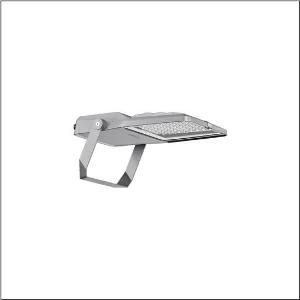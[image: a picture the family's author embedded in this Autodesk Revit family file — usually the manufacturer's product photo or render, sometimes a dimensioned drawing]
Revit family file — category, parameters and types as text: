
# Revit family: floodlight_fl_21_mini___pl52_5xa7775b2d1a_29c3
name_source: partatom
category: Lighting Fixtures
units: mm (PartAtom-declared; Revit-internal decimal feet)

## family parameters
Cut with Voids When Loaded = No
Host = Face
Light Source = No
Part Type = Normal
Room Calculation Point = No
Round Connector Dimension = Use Diameter
Shared = No

## types (1)
- --- (1 x LED, 6230 lm, 45.7 W, 3000K)
    Apparent Load = 46 VA
    CIE Flux Codes = 26 60 98 100 100
    Color Rendering = 70
    Color Temperature = 3000K
    Default Elevation = 1800 mm
    Description = Floodlight FL 21 mini, floodlight, primary light control with lens, of PMMA, primary optical cover: protective disc, of toughened safety glass, transparent, light distribution: PL52, light emission: direct distribution, installation type: surface-mounted, LED, High Power LED, rated luminous flux: 6.230lm, luminous efficacy: 136lm/W, light colour: 730, colour temperature: 3000K, control: flexible luminous flux parameterisation, time-dependent luminous flux control, constant luminous flux control, overheat protection, presetting dimming logarithmic, with terminal, 6-pole, mains connection: 220..240V, AC, 50/60Hz, start of lifetime: 46W, end of service life: 48W, reduction: 22W, luminaire housing, of diecast aluminium, powder-coated, Siteco® metallic grey (DB 702S), corrosivity category C5 mid according to DIN EN ISO 12944, sealing non-destructively replaceable, mounting bracket, of steel, galvanised, powder-coated, Siteco® metallic grey (DB 702S), Smart Interface above, protection rating (complete): IP66, insulation class (complete): insulation class II (safety insulation), certification: CE, ENEC, VDE, protection symbol: D, impact resistance: IK08, permissible operating ambient temperature: -40..+40°C, permissible operating ambient temperature for outdoor applications: -40..+50°C, standard: DIN EN 12944, LABS conformity tested according to VDMA 24364:2018-05, packaging unit: 1 piece

Light Distribution: PL52
    Height = 70 mm
    Lamp = 1 x LED
    Lamp Light Flux = 6230 lm
    Lamp Power = 45.7 W
    Lamp count = 1
    Length = 485 mm
    Luminous efficacy = 136 lm/W
    Manufacturer = Siteco
    ModVariant = No
    Model = 5XA7775B2D1A
    Number of Poles = 1
    OnlyDefault = Yes
    Power Factor = 1
    Product Name = Floodlight FL 21 mini | PL52
    Product group = floodlight | pylon annexe
    ProductGroupID = 6200
    Protection Class = Protection class II
    Protection Degree = IP 66
    RLX_Detail_Level = 1
    RLX_Emergency_Light_Flux = 0 lm
    RLX_Emergency_Type = 0
    RLX_Emergency_Type_DB = No
    RlxData = <blob elided: 96005 chars, md5=c4c7d48e>
    Socket = socket
    Standby Power = 0 W
    System Light Flux = 6230 lm
    System Power = 46 W
    Type Comments = factory setting: luminous flux: 100 % | dim-lin: 254 | 463 mA
    Type Image = l_1006845.jpg
    URL = http://relux.com
    VarID = @adj_095787
    Voltage = 0 V
    Weight = 0.00 kg
    Width = 337 mm

## geometry (parser evidence)
native form markers: Blend x4, Sweep x11
no freeform markers — native parametric forms only
